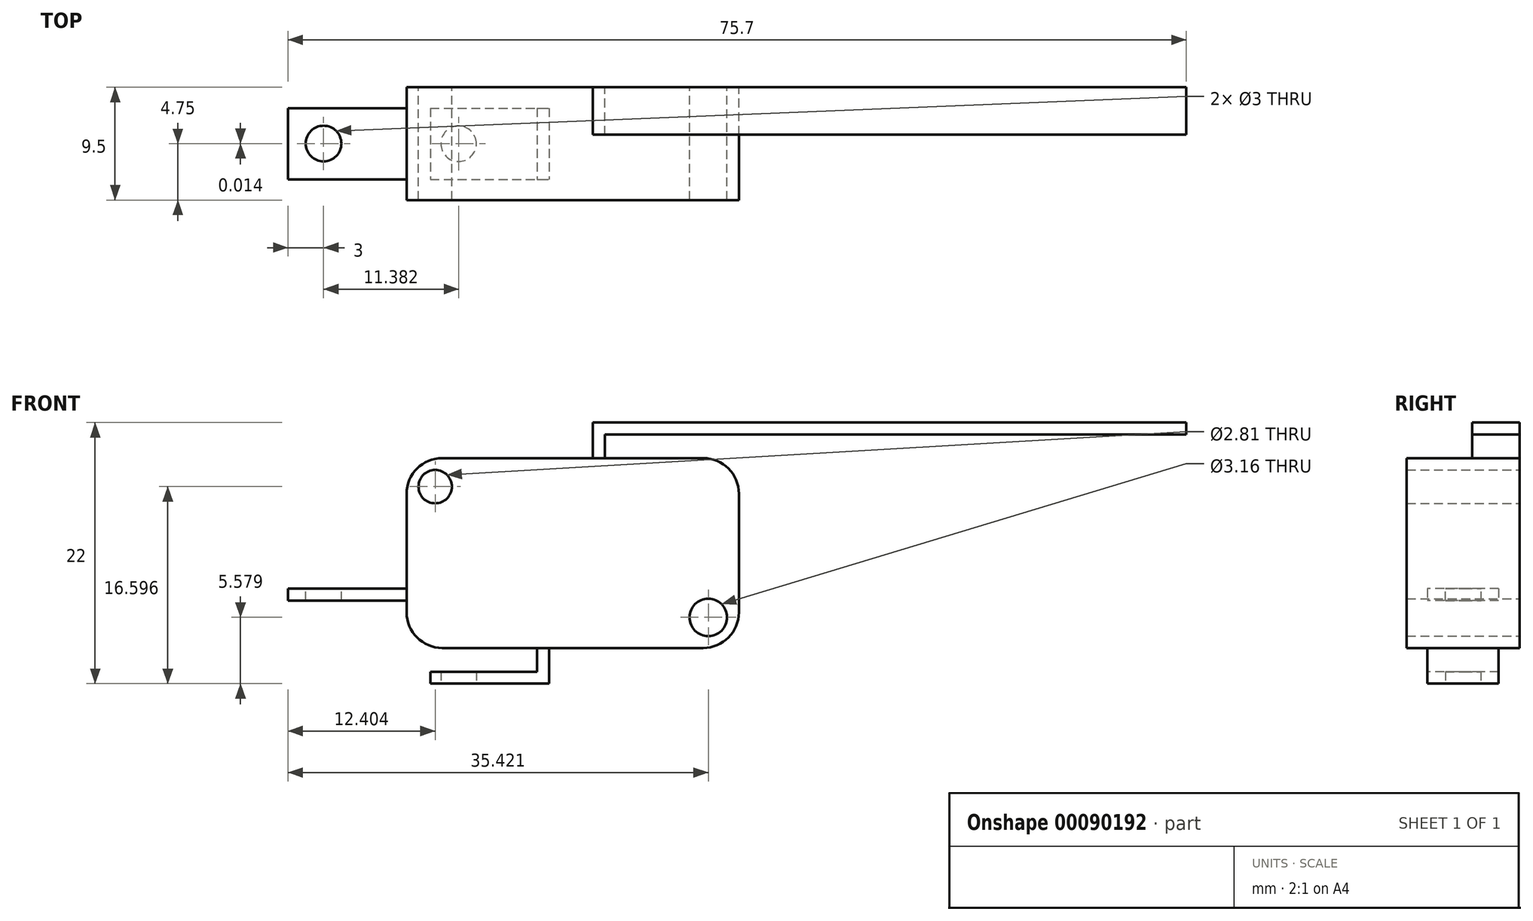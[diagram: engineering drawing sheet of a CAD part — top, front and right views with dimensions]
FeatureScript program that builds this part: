
annotation { "Feature Type Name" : "Feature", "Feature Type Description" : "" }
export const myFeature = defineFeature(function(context is Context, id is Id, definition is map)
    precondition{}
    {
        {
            var Q0;
            Q0=qCreatedBy(makeId("Front.planeOp"),FACE);
            var sketch = newSketch(context, id + "F0", { "sketchPlane" : qUnion([Q0])});
            skLineSegment(sketch, "E0.bottom", {"start": v(3, 0) * mm, "end": v(25, 0) * mm});
            skLineSegment(sketch, "E0.top", {"start": v(3, -16) * mm, "end": v(25, -16) * mm});
            skLineSegment(sketch, "E0.left", {"start": v(0, -3) * mm, "end": v(0, -13) * mm});
            skLineSegment(sketch, "E0.right", {"start": v(28, -3) * mm, "end": v(28, -13) * mm});
            skCircle(sketch, "E1", {"center": v(2.4, -2.4) * mm, "radius": 1.4 * mm});
            skCircle(sketch, "E2", {"center": v(25.42, -13.42) * mm, "radius": 1.58 * mm});
            skPoint(sketch, "E3.visualSharp", {"position": v(0, 0) * mm});
            skArc(sketch, "E3.filletArc", {"start": v(3, 0) * mm, "mid": v(0.88, -0.88) * mm, "end": v(0, -3) * mm});
            skPoint(sketch, "E4.visualSharp", {"position": v(28, -16) * mm});
            skArc(sketch, "E4.filletArc", {"start": v(25, -16) * mm, "mid": v(27.12, -15.12) * mm, "end": v(28, -13) * mm});
            skPoint(sketch, "E5.visualSharp", {"position": v(28, 0) * mm});
            skArc(sketch, "E5.filletArc", {"start": v(28, -3) * mm, "mid": v(27.12, -0.88) * mm, "end": v(25, 0) * mm});
            skPoint(sketch, "E6.visualSharp", {"position": v(0, -16) * mm});
            skArc(sketch, "E6.filletArc", {"start": v(0, -13) * mm, "mid": v(0.88, -15.12) * mm, "end": v(3, -16) * mm});
            skSolve(sketch);
        }
        {
            var Q0;
            Q0=makeQuery(id+"F0.imprint","IMPRINT",FACE,{"disambiguationData":[TD([[makeQuery(id+"F0.imprint","IMPRINT",EDGE,{"derivedFrom":sQuery(id+"F0.wireOp",EDGE,"E0.bottom")}),-1.0]])]});
            extrude(context, id + "F1", {"entities" : qUnion([Q0]), "depth" : 9.5 * mm});
        }
        {
            var Q0;
            Q0=makeQuery(id+"F1.opExtrude","SWEPT_FACE",FACE,{"disambiguationData":[OSD([sQuery(id+"F0.wireOp",EDGE,"E0.left")])]});
            var sketch = newSketch(context, id + "F2", { "sketchPlane" : qUnion([Q0])});
            skLineSegment(sketch, "E7.bottom", {"start": v(1.75, -11) * mm, "end": v(7.75, -11) * mm});
            skLineSegment(sketch, "E7.top", {"start": v(1.75, -12) * mm, "end": v(7.75, -12) * mm});
            skLineSegment(sketch, "E7.left", {"start": v(1.75, -11) * mm, "end": v(1.75, -12) * mm});
            skLineSegment(sketch, "E7.right", {"start": v(7.75, -11) * mm, "end": v(7.75, -12) * mm});
            skSolve(sketch);
        }
        {
            var Q0;
            Q0=makeQuery(id+"F2.imprint","IMPRINT",FACE,{"disambiguationData":[TD([[makeQuery(id+"F2.imprint","IMPRINT",EDGE,{"derivedFrom":sQuery(id+"F2.wireOp",EDGE,"E7.bottom")}),-1.0]])]});
            extrude(context, id + "F3", {"entities" : qUnion([Q0]), "operationType" : NewBodyOperationType.ADD, "depth" : 10 * mm});
        }
        {
            var Q0;
            Q0=makeQuery(id+"F3.opExtrude","SWEPT_FACE",FACE,{"disambiguationData":[OSD([sQuery(id+"F2.wireOp",EDGE,"E7.bottom")])]});
            var sketch = newSketch(context, id + "F4", { "sketchPlane" : qUnion([Q0])});
            skCircle(sketch, "E8", {"center": v(-7, -4.74) * mm, "radius": 1.5 * mm});
            skSolve(sketch);
        }
        {
            var Q0;
            Q0=makeQuery(id+"F4.imprint","IMPRINT",FACE,{"disambiguationData":[TD([[makeQuery(id+"F4.imprint","IMPRINT",EDGE,{"derivedFrom":sQuery(id+"F4.wireOp",EDGE,"E8")}),1.0]])]});
            extrude(context, id + "F5", {"entities" : qUnion([Q0]), "operationType" : NewBodyOperationType.REMOVE, "oppositeDirection" : true, "depth" : 25 * mm});
        }
        {
            var Q0;
            Q0=makeQuery(id+"F1.opExtrude","SWEPT_FACE",FACE,{"disambiguationData":[OSD([sQuery(id+"F0.wireOp",EDGE,"E0.top")])]});
            var sketch = newSketch(context, id + "F6", { "sketchPlane" : qUnion([Q0])});
            skLineSegment(sketch, "E9.bottom", {"start": v(11, 1.75) * mm, "end": v(12, 1.75) * mm});
            skLineSegment(sketch, "E9.top", {"start": v(11, 7.75) * mm, "end": v(12, 7.75) * mm});
            skLineSegment(sketch, "E9.left", {"start": v(11, 1.75) * mm, "end": v(11, 7.75) * mm});
            skLineSegment(sketch, "E9.right", {"start": v(12, 1.75) * mm, "end": v(12, 7.75) * mm});
            skSolve(sketch);
        }
        {
            var Q0;
            Q0=makeQuery(id+"F6.imprint","IMPRINT",FACE,{"disambiguationData":[TD([[makeQuery(id+"F6.imprint","IMPRINT",EDGE,{"derivedFrom":sQuery(id+"F6.wireOp",EDGE,"E9.bottom")}),1.0]])]});
            extrude(context, id + "F7", {"entities" : qUnion([Q0]), "operationType" : NewBodyOperationType.ADD, "depth" : 3 * mm});
        }
        {
            var Q0;
            Q0=makeQuery(id+"F7.opExtrude","SWEPT_FACE",FACE,{"disambiguationData":[OSD([sQuery(id+"F6.wireOp",EDGE,"E9.left")])]});
            var sketch = newSketch(context, id + "F8", { "sketchPlane" : qUnion([Q0])});
            skLineSegment(sketch, "E10.bottom", {"start": v(1.75, -19) * mm, "end": v(7.75, -19) * mm});
            skLineSegment(sketch, "E10.top", {"start": v(1.75, -18) * mm, "end": v(7.75, -18) * mm});
            skLineSegment(sketch, "E10.left", {"start": v(1.75, -19) * mm, "end": v(1.75, -18) * mm});
            skLineSegment(sketch, "E10.right", {"start": v(7.75, -19) * mm, "end": v(7.75, -18) * mm});
            skSolve(sketch);
        }
        {
            var Q0;
            Q0=makeQuery(id+"F8.imprint","IMPRINT",FACE,{"disambiguationData":[TD([[makeQuery(id+"F8.imprint","IMPRINT",EDGE,{"derivedFrom":sQuery(id+"F8.wireOp",EDGE,"E10.bottom")}),1.0]])]});
            extrude(context, id + "F9", {"entities" : qUnion([Q0]), "operationType" : NewBodyOperationType.ADD, "depth" : 9 * mm});
        }
        {
            var Q0;
            Q0=makeQuery(id+"F9.boolean.opBoolean","MERGE",FACE,{"derivedFrom":[makeQuery(id+"F7.opExtrude","CAP_FACE",FACE,{"disambiguationData":[OSD([sQuery(id+"F6.wireOp",EDGE,"E9.bottom"),sQuery(id+"F6.wireOp",EDGE,"E9.top"),sQuery(id+"F6.wireOp",EDGE,"E9.left"),sQuery(id+"F6.wireOp",EDGE,"E9.right")])],"isStart":false}),makeQuery(id+"F9.opExtrude","SWEPT_FACE",FACE,{"disambiguationData":[OSD([sQuery(id+"F8.wireOp",EDGE,"E10.bottom")])]})]});
            var sketch = newSketch(context, id + "F10", { "sketchPlane" : qUnion([Q0])});
            skCircle(sketch, "E11", {"center": v(4.38, 4.75) * mm, "radius": 1.5 * mm});
            skSolve(sketch);
        }
        {
            var Q0;
            Q0=makeQuery(id+"F10.imprint","IMPRINT",FACE,{"disambiguationData":[TD([[makeQuery(id+"F10.imprint","IMPRINT",EDGE,{"derivedFrom":sQuery(id+"F10.wireOp",EDGE,"E11")}),1.0]])]});
            extrude(context, id + "F11", {"entities" : qUnion([Q0]), "operationType" : NewBodyOperationType.REMOVE, "oppositeDirection" : true, "depth" : 1 * mm});
        }
        {
            var Q0;
            Q0=makeQuery(id+"F1.opExtrude","CAP_FACE",FACE,{"disambiguationData":[OSD([sQuery(id+"F0.wireOp",EDGE,"E0.bottom"),sQuery(id+"F0.wireOp",EDGE,"E0.top"),sQuery(id+"F0.wireOp",EDGE,"E0.left"),sQuery(id+"F0.wireOp",EDGE,"E0.right"),sQuery(id+"F0.wireOp",EDGE,"E1"),sQuery(id+"F0.wireOp",EDGE,"E2"),sQuery(id+"F0.wireOp",EDGE,"E3.filletArc"),sQuery(id+"F0.wireOp",EDGE,"E4.filletArc"),sQuery(id+"F0.wireOp",EDGE,"E5.filletArc"),sQuery(id+"F0.wireOp",EDGE,"E6.filletArc")])],"isStart":true});
            var sketch = newSketch(context, id + "F12", { "sketchPlane" : qUnion([Q0])});
            skLineSegment(sketch, "E12.bottom", {"start": v(-15.7, 0) * mm, "end": v(-16.7, 0) * mm});
            skLineSegment(sketch, "E12.top", {"start": v(-15.7, 2) * mm, "end": v(-16.7, 2) * mm});
            skLineSegment(sketch, "E12.left", {"start": v(-15.7, 0) * mm, "end": v(-15.7, 2) * mm});
            skLineSegment(sketch, "E12.right", {"start": v(-16.7, 0) * mm, "end": v(-16.7, 2) * mm});
            skLineSegment(sketch, "E13.bottom", {"start": v(-15.7, 2) * mm, "end": v(-65.7, 2) * mm});
            skLineSegment(sketch, "E13.top", {"start": v(-15.7, 3) * mm, "end": v(-65.7, 3) * mm});
            skLineSegment(sketch, "E13.left", {"start": v(-15.7, 2) * mm, "end": v(-15.7, 3) * mm});
            skLineSegment(sketch, "E13.right", {"start": v(-65.7, 2) * mm, "end": v(-65.7, 3) * mm});
            skSolve(sketch);
        }
        {
            var Q0;
            Q0=makeQuery(id+"F12.imprint","IMPRINT",FACE,{"disambiguationData":[TD([[makeQuery(id+"F12.imprint","IMPRINT",EDGE,{"derivedFrom":sQuery(id+"F12.wireOp",EDGE,"E13.top")}),1.0]])]});
            var Q1;
            Q1=makeQuery(id+"F12.imprint","IMPRINT",FACE,{"disambiguationData":[TD([[makeQuery(id+"F12.imprint","IMPRINT",EDGE,{"derivedFrom":sQuery(id+"F12.wireOp",EDGE,"E12.bottom")}),-1.0]])]});
            extrude(context, id + "F13", {"entities" : qUnion([Q0, Q1]), "oppositeDirection" : true, "depth" : 4 * mm});
        }
    });
